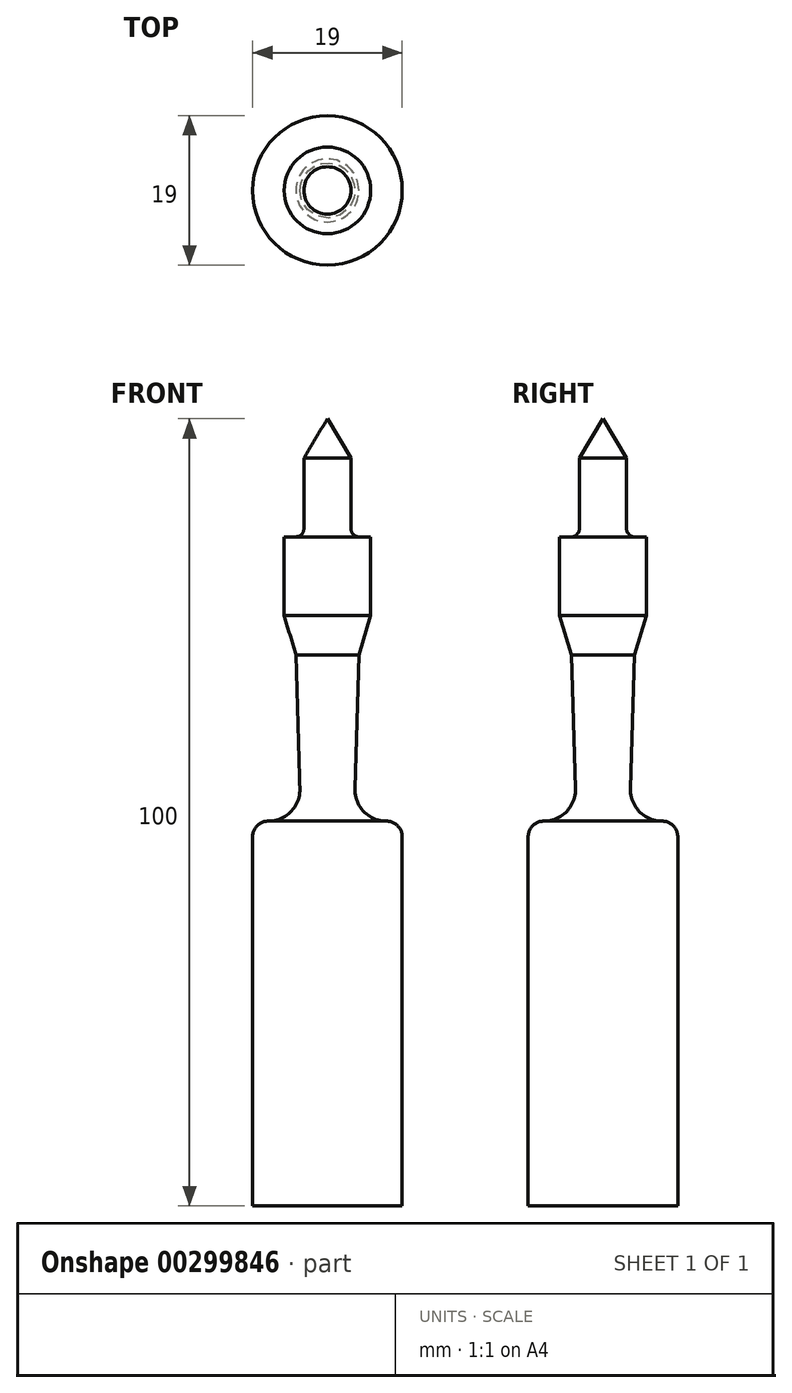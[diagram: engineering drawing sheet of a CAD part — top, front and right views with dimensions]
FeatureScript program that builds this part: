
annotation { "Feature Type Name" : "Feature", "Feature Type Description" : "" }
export const myFeature = defineFeature(function(context is Context, id is Id, definition is map)
    precondition{}
    {
        {
            var Q0;
            Q0=qCreatedBy(makeId("Front.planeOp"),FACE);
            var sketch = newSketch(context, id + "F0", { "sketchPlane" : qUnion([Q0])});
            skLineSegment(sketch, "E0", {"start": v(0, 0) * mm, "end": v(-5, 3) * mm});
            skLineSegment(sketch, "E1", {"start": v(-5, 3) * mm, "end": v(-14, 3) * mm});
            skLineSegment(sketch, "E2", {"start": v(-15, 5.5) * mm, "end": v(-25, 5.5) * mm});
            skLineSegment(sketch, "E3", {"start": v(-25, 5.5) * mm, "end": v(-30, 4) * mm});
            skLineSegment(sketch, "E4", {"start": v(-30, 4) * mm, "end": v(-47, 3.5) * mm});
            skArc(sketch, "E5", {"start": v(-51.12, 7.5) * mm, "mid": v(-49.9, 4.63) * mm, "end": v(-47, 3.5) * mm});
            skLineSegment(sketch, "E6", {"start": v(-53.12, 9.5) * mm, "end": v(-100, 9.5) * mm});
            skLineSegment(sketch, "E7", {"start": v(-100, 9.5) * mm, "end": v(-100, 0) * mm});
            skLineSegment(sketch, "E8", {"start": v(-100, 0) * mm, "end": v(0, 0) * mm});
            skArc(sketch, "E9", {"start": v(-15, 4) * mm, "mid": v(-14.7, 3.3) * mm, "end": v(-14, 3) * mm});
            skLineSegment(sketch, "E10", {"start": v(-15, 4) * mm, "end": v(-15, 5.5) * mm});
            skArc(sketch, "E11", {"start": v(-51.12, 7.5) * mm, "mid": v(-51.7, 8.91) * mm, "end": v(-53.12, 9.5) * mm});
            skSolve(sketch);
        }
        {
            var Q0;
            Q0=makeQuery(id+"F0.imprint","IMPRINT",FACE,{"disambiguationData":[TD([[makeQuery(id+"F0.imprint","IMPRINT",EDGE,{"derivedFrom":sQuery(id+"F0.wireOp",EDGE,"E0")}),1.0]])]});
            var Q1;
            Q1=sQuery(id+"F0.wireOp",EDGE,"E8");
            revolve(context, id + "F1", {"entities" : qUnion([Q0]), "axis" : qUnion([Q1]), "revolveType" : RevolveType.FULL});
        }
        {
            var Q0;
            Q0=qCreatedBy(makeId("Right.planeOp"),FACE);
            var sketch = newSketch(context, id + "F2", { "sketchPlane" : qUnion([Q0])});
            skLineSegment(sketch, "E12", {"start": v(9.5, 0) * mm, "end": v(-118.26, 0) * mm});
            skSolve(sketch);
        }
        {
            var Q0;
            Q0=makeQuery(id+"F1.opRevolve","SWEPT_BODY",BODY,{"disambiguationData":[OSD([sQuery(id+"F0.wireOp",EDGE,"E0"),sQuery(id+"F0.wireOp",EDGE,"E1"),sQuery(id+"F0.wireOp",EDGE,"E2"),sQuery(id+"F0.wireOp",EDGE,"E3"),sQuery(id+"F0.wireOp",EDGE,"E4"),sQuery(id+"F0.wireOp",EDGE,"E5"),sQuery(id+"F0.wireOp",EDGE,"E6"),sQuery(id+"F0.wireOp",EDGE,"E7"),sQuery(id+"F0.wireOp",EDGE,"E8"),sQuery(id+"F0.wireOp",EDGE,"E9"),sQuery(id+"F0.wireOp",EDGE,"E10"),sQuery(id+"F0.wireOp",EDGE,"E11")])]});
            var Q1;
            Q1=sQuery(id+"F2.wireOp",EDGE,"E12");
            transform(context, id + "F3", {"entities" : qUnion([Q0]), "transformType" : TransformType.ROTATION, "transformAxis" : qUnion([Q1]), "angle" : 90 * degree, "makeCopy" : false});
        }
    });
